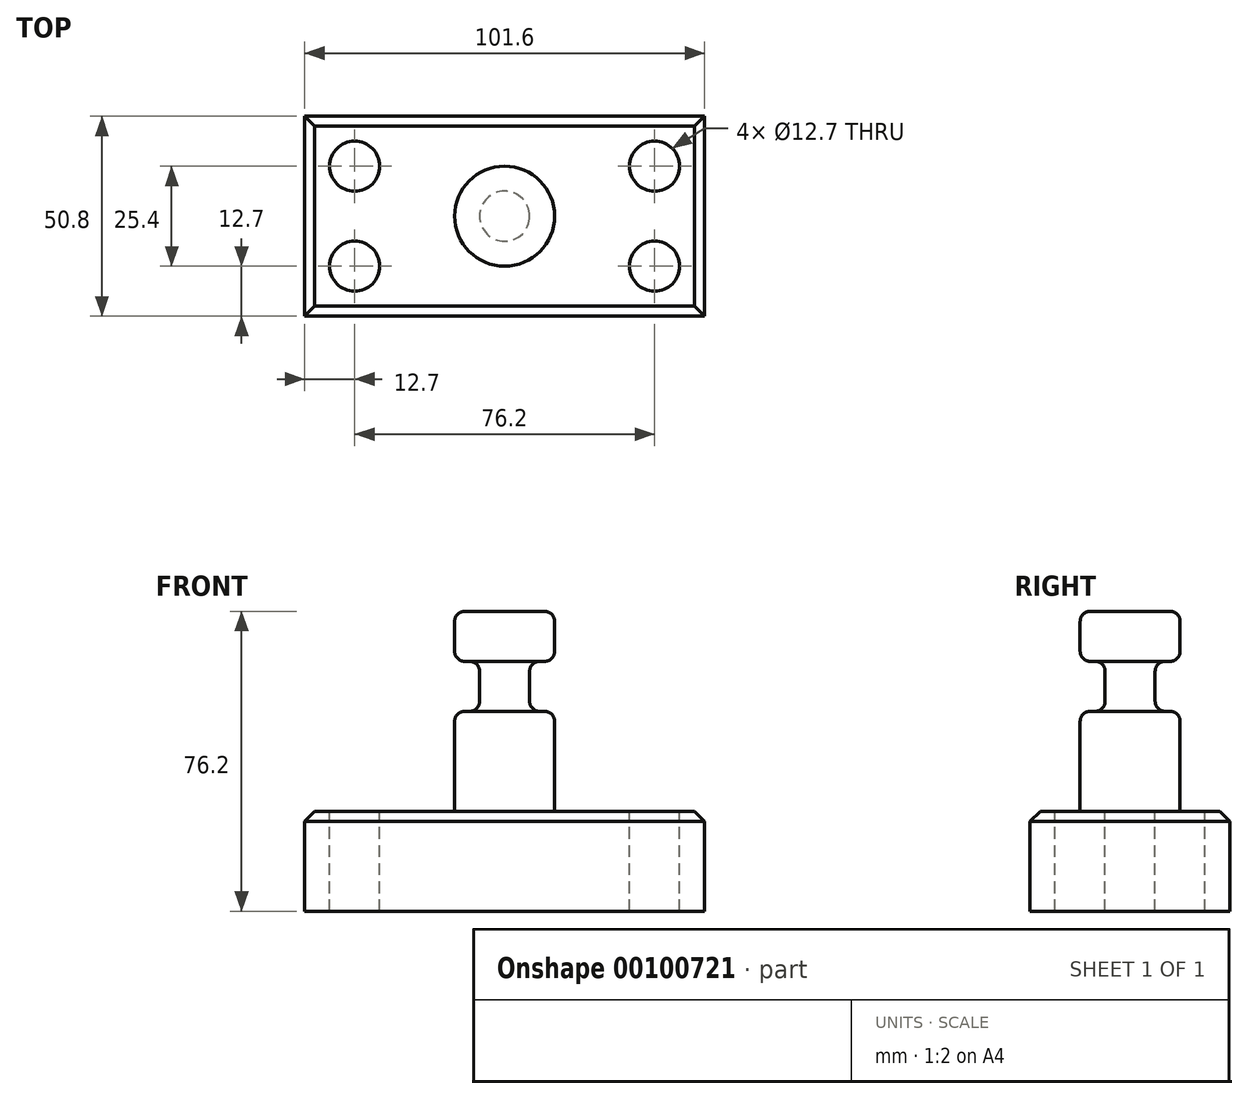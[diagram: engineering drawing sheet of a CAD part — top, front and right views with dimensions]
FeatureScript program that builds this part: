
annotation { "Feature Type Name" : "Feature", "Feature Type Description" : "" }
export const myFeature = defineFeature(function(context is Context, id is Id, definition is map)
    precondition{}
    {
        {
            var Q0;
            Q0=qCreatedBy(makeId("Top.planeOp"),FACE);
            var sketch = newSketch(context, id + "F0", { "sketchPlane" : qUnion([Q0])});
            skLineSegment(sketch, "E0.bottom", {"start": v(-50.8, 25.4) * mm, "end": v(50.8, 25.4) * mm});
            skLineSegment(sketch, "E0.top", {"start": v(-50.8, -25.4) * mm, "end": v(50.8, -25.4) * mm});
            skLineSegment(sketch, "E0.left", {"start": v(-50.8, 25.4) * mm, "end": v(-50.8, -25.4) * mm});
            skLineSegment(sketch, "E0.right", {"start": v(50.8, 25.4) * mm, "end": v(50.8, -25.4) * mm});
            skPoint(sketch, "E0.middle", {"position": v(0, 0) * mm});
            skSolve(sketch);
        }
        {
            var Q0;
            Q0=makeQuery(id+"F0.imprint","IMPRINT",FACE,{"disambiguationData":[TD([[makeQuery(id+"F0.imprint","IMPRINT",EDGE,{"derivedFrom":sQuery(id+"F0.wireOp",EDGE,"E0.bottom")}),-1.0]])]});
            extrude(context, id + "F1", {"entities" : qUnion([Q0]), "depth" : 25.4 * mm});
        }
        {
            var Q0;
            Q0=makeQuery(id+"F1.opExtrude","CAP_FACE",FACE,{"disambiguationData":[OSD([sQuery(id+"F0.wireOp",EDGE,"E0.bottom"),sQuery(id+"F0.wireOp",EDGE,"E0.top"),sQuery(id+"F0.wireOp",EDGE,"E0.left"),sQuery(id+"F0.wireOp",EDGE,"E0.right")])],"isStart":false});
            var sketch = newSketch(context, id + "F2", { "sketchPlane" : qUnion([Q0])});
            skCircle(sketch, "E1", {"center": v(38.1, -12.7) * mm, "radius": 6.35 * mm});
            skCircle(sketch, "E2", {"center": v(-38.1, -12.7) * mm, "radius": 6.35 * mm});
            skCircle(sketch, "E3", {"center": v(-38.1, 12.7) * mm, "radius": 6.35 * mm});
            skCircle(sketch, "E4", {"center": v(38.1, 12.7) * mm, "radius": 6.35 * mm});
            skSolve(sketch);
        }
        {
            var Q0;
            Q0=qCreatedBy(makeId("Front.planeOp"),FACE);
            var sketch = newSketch(context, id + "F3", { "sketchPlane" : qUnion([Q0])});
            skLineSegment(sketch, "E5.bottom", {"start": v(0, 76.2) * mm, "end": v(-12.7, 76.2) * mm});
            skLineSegment(sketch, "E5.top", {"start": v(0, 25.4) * mm, "end": v(-12.7, 25.4) * mm});
            skLineSegment(sketch, "E5.left", {"start": v(0, 76.2) * mm, "end": v(0, 25.4) * mm});
            skLineSegment(sketch, "E5.right", {"start": v(-12.7, 76.2) * mm, "end": v(-12.7, 25.4) * mm});
            skSolve(sketch);
        }
        {
            var Q0;
            Q0 = qSketchRegion(id + "F3", true);
            var Q1;
            Q1=sQuery(id+"F3.wireOp",EDGE,"E5.left");
            revolve(context, id + "F4", {"operationType" : NewBodyOperationType.ADD, "entities" : qUnion([Q0]), "axis" : qUnion([Q1]), "revolveType" : RevolveType.FULL});
        }
        {
            var Q0;
            Q0=makeQuery(id+"F2.imprint","IMPRINT",FACE,{"disambiguationData":[TD([[makeQuery(id+"F2.imprint","IMPRINT",EDGE,{"derivedFrom":sQuery(id+"F2.wireOp",EDGE,"E1")}),1.0]])]});
            var Q1;
            Q1=makeQuery(id+"F2.imprint","IMPRINT",FACE,{"disambiguationData":[TD([[makeQuery(id+"F2.imprint","IMPRINT",EDGE,{"derivedFrom":sQuery(id+"F2.wireOp",EDGE,"E3")}),1.0]])]});
            var Q2;
            Q2=makeQuery(id+"F2.imprint","IMPRINT",FACE,{"disambiguationData":[TD([[makeQuery(id+"F2.imprint","IMPRINT",EDGE,{"derivedFrom":sQuery(id+"F2.wireOp",EDGE,"E4")}),1.0]])]});
            var Q3;
            Q3=makeQuery(id+"F2.imprint","IMPRINT",FACE,{"disambiguationData":[TD([[makeQuery(id+"F2.imprint","IMPRINT",EDGE,{"derivedFrom":sQuery(id+"F2.wireOp",EDGE,"E2")}),1.0]])]});
            extrude(context, id + "F5", {"entities" : qUnion([Q0, Q1, Q2, Q3]), "operationType" : NewBodyOperationType.REMOVE, "endBound" : BoundingType.THROUGH_ALL, "oppositeDirection" : true, "depth" : 25.4 * mm});
        }
        {
            var Q0;
            Q0=qCreatedBy(makeId("Front.planeOp"),FACE);
            var sketch = newSketch(context, id + "F6", { "sketchPlane" : qUnion([Q0])});
            skLineSegment(sketch, "E6.bottom", {"start": v(-15.27, 63.5) * mm, "end": v(-6.35, 63.5) * mm});
            skLineSegment(sketch, "E6.top", {"start": v(-15.27, 50.8) * mm, "end": v(-6.35, 50.8) * mm});
            skLineSegment(sketch, "E6.left", {"start": v(-15.27, 63.5) * mm, "end": v(-15.27, 50.8) * mm});
            skLineSegment(sketch, "E6.right", {"start": v(-6.35, 63.5) * mm, "end": v(-6.35, 50.8) * mm});
            skLineSegment(sketch, "E7", {"start": v(0, 0) * mm, "end": v(0, 87.04) * mm, "construction": true});
            skSolve(sketch);
        }
        {
            var Q0;
            Q0=makeQuery(id+"F6.imprint","IMPRINT",FACE,{"disambiguationData":[TD([[makeQuery(id+"F6.imprint","IMPRINT",EDGE,{"derivedFrom":sQuery(id+"F6.wireOp",EDGE,"E6.bottom")}),-1.0]])]});
            var Q1;
            Q1=sQuery(id+"F6.wireOp",EDGE,"E7");
            revolve(context, id + "F7", {"operationType" : NewBodyOperationType.REMOVE, "entities" : qUnion([Q0]), "axis" : qUnion([Q1]), "revolveType" : RevolveType.FULL, "oppositeDirection" : true});
        }
        {
            var Q0;
            Q0=makeQuery(id+"F7.boolean.opBoolean","INTERSECT",EDGE,{"derivedFrom":[makeQuery(id+"F4.opRevolve","SWEPT_FACE",FACE,{"disambiguationData":[OSD([sQuery(id+"F3.wireOp",EDGE,"E5.right")])]}),makeQuery(id+"F7.opRevolve","SWEPT_FACE",FACE,{"disambiguationData":[OSD([sQuery(id+"F6.wireOp",EDGE,"E6.top")])]})]});
            var Q1;
            Q1=makeQuery(id+"F4.opRevolve","SWEPT_EDGE",EDGE,{"disambiguationData":[OSD([sQuery(id+"F3.wireOp",EDGE,"E5.top"),sQuery(id+"F3.wireOp",EDGE,"E5.right")])]});
            var Q2;
            Q2=makeQuery(id+"F7.boolean.opBoolean","COPY",EDGE,{"derivedFrom":makeQuery(id+"F7.opRevolve","SWEPT_EDGE",EDGE,{"disambiguationData":[OSD([sQuery(id+"F6.wireOp",EDGE,"E6.top"),sQuery(id+"F6.wireOp",EDGE,"E6.right")])]})});
            var Q3;
            Q3=makeQuery(id+"F7.boolean.opBoolean","COPY",EDGE,{"derivedFrom":makeQuery(id+"F7.opRevolve","SWEPT_EDGE",EDGE,{"disambiguationData":[OSD([sQuery(id+"F6.wireOp",EDGE,"E6.bottom"),sQuery(id+"F6.wireOp",EDGE,"E6.right")])]})});
            var Q4;
            Q4=makeQuery(id+"F7.boolean.opBoolean","INTERSECT",EDGE,{"derivedFrom":[makeQuery(id+"F4.opRevolve","SWEPT_FACE",FACE,{"disambiguationData":[OSD([sQuery(id+"F3.wireOp",EDGE,"E5.right")])]}),makeQuery(id+"F7.opRevolve","SWEPT_FACE",FACE,{"disambiguationData":[OSD([sQuery(id+"F6.wireOp",EDGE,"E6.bottom")])]})]});
            var Q5;
            Q5=makeQuery(id+"F4.opRevolve","SWEPT_EDGE",EDGE,{"disambiguationData":[OSD([sQuery(id+"F3.wireOp",EDGE,"E5.bottom"),sQuery(id+"F3.wireOp",EDGE,"E5.right")])]});
            fillet(context, id + "F8", {"entities" : qUnion([Q0, Q1, Q2, Q3, Q4, Q5]), "radius" : 2.54 * mm, "tangentPropagation" : true, "allowEdgeOverflow" : false});
        }
        {
            var Q0;
            Q0=makeQuery(id+"F1.opExtrude","CAP_EDGE",EDGE,{"disambiguationData":[OSD([sQuery(id+"F0.wireOp",EDGE,"E0.top")])],"isStart":false});
            var Q1;
            Q1=makeQuery(id+"F1.opExtrude","CAP_EDGE",EDGE,{"disambiguationData":[OSD([sQuery(id+"F0.wireOp",EDGE,"E0.left")])],"isStart":false});
            var Q2;
            Q2=makeQuery(id+"F1.opExtrude","CAP_EDGE",EDGE,{"disambiguationData":[OSD([sQuery(id+"F0.wireOp",EDGE,"E0.bottom")])],"isStart":false});
            var Q3;
            Q3=makeQuery(id+"F1.opExtrude","CAP_EDGE",EDGE,{"disambiguationData":[OSD([sQuery(id+"F0.wireOp",EDGE,"E0.right")])],"isStart":false});
            chamfer(context, id + "F9", {"entities" : qUnion([Q0, Q1, Q2, Q3]), "width" : 2.54 * mm, "tangentPropagation" : true});
        }
    });
